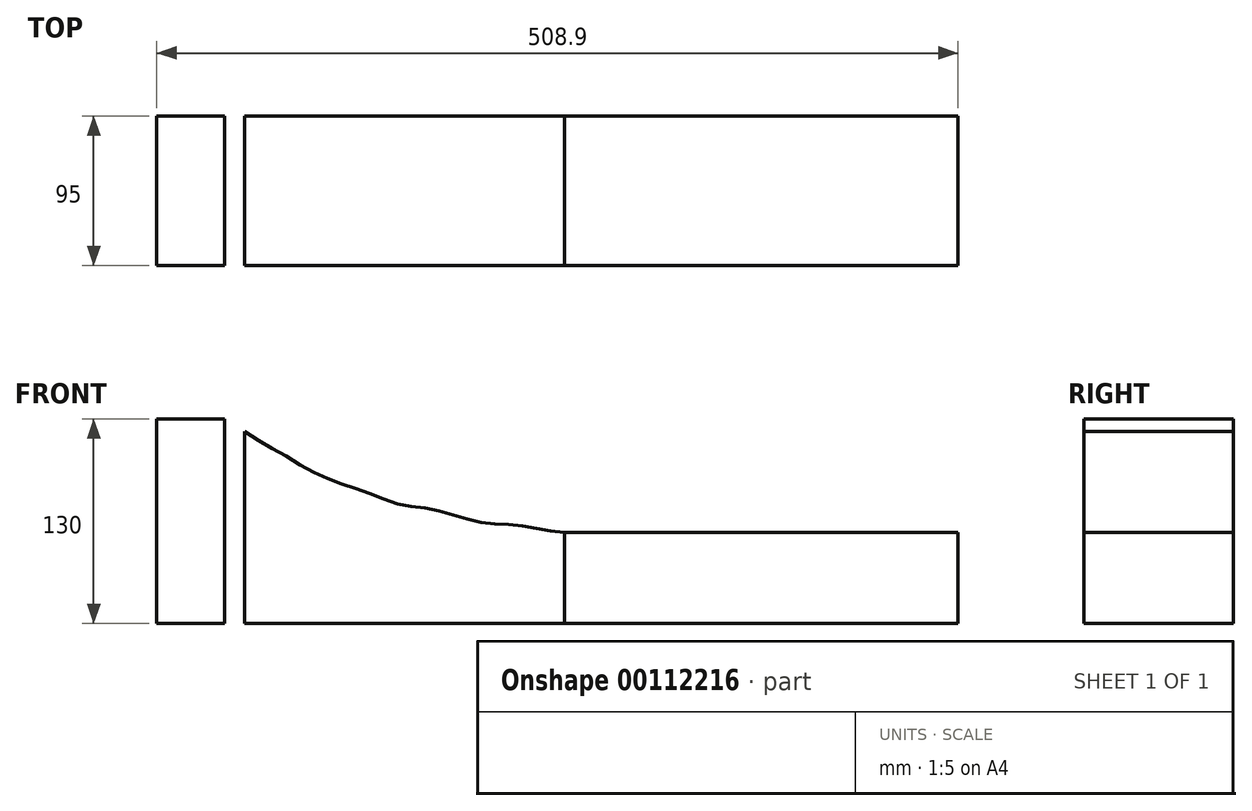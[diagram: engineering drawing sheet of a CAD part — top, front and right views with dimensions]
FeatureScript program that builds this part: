
annotation { "Feature Type Name" : "Feature", "Feature Type Description" : "" }
export const myFeature = defineFeature(function(context is Context, id is Id, definition is map)
    precondition{}
    {
        {
            var Q0;
            Q0=qCreatedBy(makeId("Right.planeOp"),FACE);
            var sketch = newSketch(context, id + "F0", { "sketchPlane" : qUnion([Q0])});
            skLineSegment(sketch, "E0.bottom", {"start": v(0, 0) * mm, "end": v(95, 0) * mm});
            skLineSegment(sketch, "E0.top", {"start": v(0, 130) * mm, "end": v(95, 130) * mm});
            skLineSegment(sketch, "E0.left", {"start": v(0, 0) * mm, "end": v(0, 130) * mm});
            skLineSegment(sketch, "E0.right", {"start": v(95, 0) * mm, "end": v(95, 130) * mm});
            skSolve(sketch);
        }
        {
            var Q0;
            Q0=makeQuery(id+"F0.imprint","IMPRINT",FACE,{"disambiguationData":[TD([[makeQuery(id+"F0.imprint","IMPRINT",EDGE,{"derivedFrom":sQuery(id+"F0.wireOp",EDGE,"E0.bottom")}),1.0]])]});
            cPlane(context, id + "F1", {"entities" : qUnion([Q0]), "cplaneType" : CPlaneType.OFFSET, "offset" : 12.7 * mm, "width" : 150 * mm, "height" : 150 * mm});
        }
        {
            var Q0;
            Q0=qCreatedBy(id+"F1.planeOp",FACE);
            cPlane(context, id + "F2", {"entities" : qUnion([Q0]), "cplaneType" : CPlaneType.OFFSET, "offset" : 12.7 * mm, "width" : 150 * mm, "height" : 150 * mm});
        }
        {
            var Q0;
            Q0=qCreatedBy(id+"F2.planeOp",FACE);
            cPlane(context, id + "F3", {"entities" : qUnion([Q0]), "cplaneType" : CPlaneType.OFFSET, "offset" : 12.7 * mm, "width" : 150 * mm, "height" : 150 * mm});
        }
        {
            var Q0;
            Q0=qCreatedBy(id+"F3.planeOp",FACE);
            cPlane(context, id + "F4", {"entities" : qUnion([Q0]), "cplaneType" : CPlaneType.OFFSET, "offset" : 12.7 * mm, "width" : 150 * mm, "height" : 150 * mm});
        }
        {
            var Q0;
            Q0=qCreatedBy(id+"F4.planeOp",FACE);
            cPlane(context, id + "F5", {"entities" : qUnion([Q0]), "cplaneType" : CPlaneType.OFFSET, "offset" : 12.7 * mm, "width" : 150 * mm, "height" : 150 * mm});
        }
        {
            var Q0;
            Q0=qCreatedBy(id+"F1.planeOp",FACE);
            var sketch = newSketch(context, id + "F6", { "sketchPlane" : qUnion([Q0])});
            skLineSegment(sketch, "E1.bottom", {"start": v(0, 0) * mm, "end": v(95, 0) * mm});
            skLineSegment(sketch, "E1.top", {"start": v(0, 122) * mm, "end": v(95, 122) * mm});
            skLineSegment(sketch, "E1.left", {"start": v(0, 0) * mm, "end": v(0, 122) * mm});
            skLineSegment(sketch, "E1.right", {"start": v(95, 0) * mm, "end": v(95, 122) * mm});
            skSolve(sketch);
        }
        {
            var Q0;
            Q0=qCreatedBy(id+"F2.planeOp",FACE);
            var sketch = newSketch(context, id + "F7", { "sketchPlane" : qUnion([Q0])});
            skLineSegment(sketch, "E2.bottom", {"start": v(0, 0) * mm, "end": v(95, 0) * mm});
            skLineSegment(sketch, "E2.top", {"start": v(0, 114) * mm, "end": v(95, 114) * mm});
            skLineSegment(sketch, "E2.left", {"start": v(0, 0) * mm, "end": v(0, 114) * mm});
            skLineSegment(sketch, "E2.right", {"start": v(95, 0) * mm, "end": v(95, 114) * mm});
            skSolve(sketch);
        }
        {
            var Q0;
            Q0=qCreatedBy(id+"F3.planeOp",FACE);
            var sketch = newSketch(context, id + "F8", { "sketchPlane" : qUnion([Q0])});
            skLineSegment(sketch, "E3.bottom", {"start": v(0, 0) * mm, "end": v(95, 0) * mm});
            skLineSegment(sketch, "E3.top", {"start": v(0, 107) * mm, "end": v(95, 107) * mm});
            skLineSegment(sketch, "E3.left", {"start": v(0, 0) * mm, "end": v(0, 107) * mm});
            skLineSegment(sketch, "E3.right", {"start": v(95, 0) * mm, "end": v(95, 107) * mm});
            skSolve(sketch);
        }
        {
            var Q0;
            Q0=qCreatedBy(id+"F4.planeOp",FACE);
            var sketch = newSketch(context, id + "F9", { "sketchPlane" : qUnion([Q0])});
            skLineSegment(sketch, "E4.bottom", {"start": v(0, 0) * mm, "end": v(95, 0) * mm});
            skLineSegment(sketch, "E4.top", {"start": v(0, 99) * mm, "end": v(95, 99) * mm});
            skLineSegment(sketch, "E4.left", {"start": v(0, 0) * mm, "end": v(0, 99) * mm});
            skLineSegment(sketch, "E4.right", {"start": v(95, 0) * mm, "end": v(95, 99) * mm});
            skSolve(sketch);
        }
        {
            var Q0;
            Q0=qCreatedBy(id+"F5.planeOp",FACE);
            var sketch = newSketch(context, id + "F10", { "sketchPlane" : qUnion([Q0])});
            skLineSegment(sketch, "E5.bottom", {"start": v(0, 0) * mm, "end": v(95, 0) * mm});
            skLineSegment(sketch, "E5.top", {"start": v(0, 93) * mm, "end": v(95, 93) * mm});
            skLineSegment(sketch, "E5.left", {"start": v(0, 0) * mm, "end": v(0, 93) * mm});
            skLineSegment(sketch, "E5.right", {"start": v(95, 0) * mm, "end": v(95, 93) * mm});
            skSolve(sketch);
        }
        {
            var Q0;
            Q0=qCreatedBy(id+"F5.planeOp",FACE);
            cPlane(context, id + "F11", {"entities" : qUnion([Q0]), "cplaneType" : CPlaneType.OFFSET, "offset" : 12.7 * mm, "width" : 150 * mm, "height" : 150 * mm});
        }
        {
            var Q0;
            Q0=qCreatedBy(id+"F11.planeOp",FACE);
            cPlane(context, id + "F12", {"entities" : qUnion([Q0]), "cplaneType" : CPlaneType.OFFSET, "offset" : 12.7 * mm, "width" : 150 * mm, "height" : 150 * mm});
        }
        {
            var Q0;
            Q0=qCreatedBy(id+"F12.planeOp",FACE);
            cPlane(context, id + "F13", {"entities" : qUnion([Q0]), "cplaneType" : CPlaneType.OFFSET, "offset" : 12.7 * mm, "width" : 150 * mm, "height" : 150 * mm});
        }
        {
            var Q0;
            Q0=qCreatedBy(id+"F11.planeOp",FACE);
            var sketch = newSketch(context, id + "F14", { "sketchPlane" : qUnion([Q0])});
            skLineSegment(sketch, "E6.bottom", {"start": v(0, 0) * mm, "end": v(95, 0) * mm});
            skLineSegment(sketch, "E6.top", {"start": v(0, 88) * mm, "end": v(95, 88) * mm});
            skLineSegment(sketch, "E6.left", {"start": v(0, 0) * mm, "end": v(0, 88) * mm});
            skLineSegment(sketch, "E6.right", {"start": v(95, 0) * mm, "end": v(95, 88) * mm});
            skSolve(sketch);
        }
        {
            var Q0;
            Q0=qCreatedBy(id+"F12.planeOp",FACE);
            var sketch = newSketch(context, id + "F15", { "sketchPlane" : qUnion([Q0])});
            skLineSegment(sketch, "E7.bottom", {"start": v(0, 0) * mm, "end": v(95, 0) * mm});
            skLineSegment(sketch, "E7.top", {"start": v(0, 84) * mm, "end": v(95, 84) * mm});
            skLineSegment(sketch, "E7.left", {"start": v(0, 0) * mm, "end": v(0, 84) * mm});
            skLineSegment(sketch, "E7.right", {"start": v(95, 0) * mm, "end": v(95, 84) * mm});
            skSolve(sketch);
        }
        {
            var Q0;
            Q0=qCreatedBy(id+"F13.planeOp",FACE);
            var sketch = newSketch(context, id + "F16", { "sketchPlane" : qUnion([Q0])});
            skLineSegment(sketch, "E8.bottom", {"start": v(0, 0) * mm, "end": v(95, 0) * mm});
            skLineSegment(sketch, "E8.top", {"start": v(0, 79) * mm, "end": v(95, 79) * mm});
            skLineSegment(sketch, "E8.left", {"start": v(0, 0) * mm, "end": v(0, 79) * mm});
            skLineSegment(sketch, "E8.right", {"start": v(95, 0) * mm, "end": v(95, 79) * mm});
            skSolve(sketch);
        }
        {
            var Q0;
            Q0=qCreatedBy(id+"F13.planeOp",FACE);
            cPlane(context, id + "F17", {"entities" : qUnion([Q0]), "cplaneType" : CPlaneType.OFFSET, "offset" : 12.7 * mm, "width" : 150 * mm, "height" : 150 * mm});
        }
        {
            var Q0;
            Q0=qCreatedBy(id+"F17.planeOp",FACE);
            cPlane(context, id + "F18", {"entities" : qUnion([Q0]), "cplaneType" : CPlaneType.OFFSET, "offset" : 12.7 * mm, "width" : 150 * mm, "height" : 150 * mm});
        }
        {
            var Q0;
            Q0=qCreatedBy(id+"F18.planeOp",FACE);
            cPlane(context, id + "F19", {"entities" : qUnion([Q0]), "cplaneType" : CPlaneType.OFFSET, "offset" : 12.7 * mm, "width" : 150 * mm, "height" : 150 * mm});
        }
        {
            var Q0;
            Q0=qCreatedBy(id+"F19.planeOp",FACE);
            cPlane(context, id + "F20", {"entities" : qUnion([Q0]), "cplaneType" : CPlaneType.OFFSET, "offset" : 12.7 * mm, "width" : 150 * mm, "height" : 150 * mm});
        }
        {
            var Q0;
            Q0=qCreatedBy(id+"F20.planeOp",FACE);
            cPlane(context, id + "F21", {"entities" : qUnion([Q0]), "cplaneType" : CPlaneType.OFFSET, "offset" : 12.7 * mm, "width" : 150 * mm, "height" : 150 * mm});
        }
        {
            var Q0;
            Q0=qCreatedBy(id+"F17.planeOp",FACE);
            var sketch = newSketch(context, id + "F22", { "sketchPlane" : qUnion([Q0])});
            skLineSegment(sketch, "E9.bottom", {"start": v(0, 0) * mm, "end": v(95, 0) * mm});
            skLineSegment(sketch, "E9.top", {"start": v(0, 75) * mm, "end": v(95, 75) * mm});
            skLineSegment(sketch, "E9.left", {"start": v(0, 0) * mm, "end": v(0, 75) * mm});
            skLineSegment(sketch, "E9.right", {"start": v(95, 0) * mm, "end": v(95, 75) * mm});
            skSolve(sketch);
        }
        {
            var Q0;
            Q0=qCreatedBy(id+"F18.planeOp",FACE);
            var sketch = newSketch(context, id + "F23", { "sketchPlane" : qUnion([Q0])});
            skLineSegment(sketch, "E10.bottom", {"start": v(0, 0) * mm, "end": v(95, 0) * mm});
            skLineSegment(sketch, "E10.top", {"start": v(0, 73.5) * mm, "end": v(95, 73.5) * mm});
            skLineSegment(sketch, "E10.left", {"start": v(0, 0) * mm, "end": v(0, 73.5) * mm});
            skLineSegment(sketch, "E10.right", {"start": v(95, 0) * mm, "end": v(95, 73.5) * mm});
            skSolve(sketch);
        }
        {
            var Q0;
            Q0=qCreatedBy(id+"F19.planeOp",FACE);
            var sketch = newSketch(context, id + "F24", { "sketchPlane" : qUnion([Q0])});
            skLineSegment(sketch, "E11.bottom", {"start": v(0, 0) * mm, "end": v(95, 0) * mm});
            skLineSegment(sketch, "E11.top", {"start": v(0, 70.5) * mm, "end": v(95, 70.5) * mm});
            skLineSegment(sketch, "E11.left", {"start": v(0, 0) * mm, "end": v(0, 70.5) * mm});
            skLineSegment(sketch, "E11.right", {"start": v(95, 0) * mm, "end": v(95, 70.5) * mm});
            skSolve(sketch);
        }
        {
            var Q0;
            Q0=qCreatedBy(id+"F20.planeOp",FACE);
            var sketch = newSketch(context, id + "F25", { "sketchPlane" : qUnion([Q0])});
            skLineSegment(sketch, "E12.bottom", {"start": v(0, 0) * mm, "end": v(95, 0) * mm});
            skLineSegment(sketch, "E12.top", {"start": v(0, 67) * mm, "end": v(95, 67) * mm});
            skLineSegment(sketch, "E12.left", {"start": v(0, 0) * mm, "end": v(0, 67) * mm});
            skLineSegment(sketch, "E12.right", {"start": v(95, 0) * mm, "end": v(95, 67) * mm});
            skSolve(sketch);
        }
        {
            var Q0;
            Q0=qCreatedBy(id+"F21.planeOp",FACE);
            var sketch = newSketch(context, id + "F26", { "sketchPlane" : qUnion([Q0])});
            skLineSegment(sketch, "E13.bottom", {"start": v(0, 0) * mm, "end": v(95, 0) * mm});
            skLineSegment(sketch, "E13.top", {"start": v(0, 64) * mm, "end": v(95, 64) * mm});
            skLineSegment(sketch, "E13.left", {"start": v(0, 0) * mm, "end": v(0, 64) * mm});
            skLineSegment(sketch, "E13.right", {"start": v(95, 0) * mm, "end": v(95, 64) * mm});
            skSolve(sketch);
        }
        {
            var Q0;
            Q0=qCreatedBy(id+"F21.planeOp",FACE);
            cPlane(context, id + "F27", {"entities" : qUnion([Q0]), "cplaneType" : CPlaneType.OFFSET, "offset" : 12.7 * mm, "width" : 150 * mm, "height" : 150 * mm});
        }
        {
            var Q0;
            Q0=qCreatedBy(id+"F27.planeOp",FACE);
            cPlane(context, id + "F28", {"entities" : qUnion([Q0]), "cplaneType" : CPlaneType.OFFSET, "offset" : 12.7 * mm, "width" : 150 * mm, "height" : 150 * mm});
        }
        {
            var Q0;
            Q0=qCreatedBy(id+"F28.planeOp",FACE);
            cPlane(context, id + "F29", {"entities" : qUnion([Q0]), "cplaneType" : CPlaneType.OFFSET, "offset" : 12.7 * mm, "width" : 150 * mm, "height" : 150 * mm});
        }
        {
            var Q0;
            Q0=qCreatedBy(id+"F29.planeOp",FACE);
            cPlane(context, id + "F30", {"entities" : qUnion([Q0]), "cplaneType" : CPlaneType.OFFSET, "offset" : 12.7 * mm, "width" : 150 * mm, "height" : 150 * mm});
        }
        {
            var Q0;
            Q0=qCreatedBy(id+"F27.planeOp",FACE);
            var sketch = newSketch(context, id + "F31", { "sketchPlane" : qUnion([Q0])});
            skLineSegment(sketch, "E14.bottom", {"start": v(0, 0) * mm, "end": v(95, 0) * mm});
            skLineSegment(sketch, "E14.top", {"start": v(0, 63) * mm, "end": v(95, 63) * mm});
            skLineSegment(sketch, "E14.left", {"start": v(0, 0) * mm, "end": v(0, 63) * mm});
            skLineSegment(sketch, "E14.right", {"start": v(95, 0) * mm, "end": v(95, 63) * mm});
            skSolve(sketch);
        }
        {
            var Q0;
            Q0=qCreatedBy(id+"F28.planeOp",FACE);
            var sketch = newSketch(context, id + "F32", { "sketchPlane" : qUnion([Q0])});
            skLineSegment(sketch, "E15.bottom", {"start": v(0, 0) * mm, "end": v(95, 0) * mm});
            skLineSegment(sketch, "E15.top", {"start": v(0, 62) * mm, "end": v(95, 62) * mm});
            skLineSegment(sketch, "E15.left", {"start": v(0, 0) * mm, "end": v(0, 62) * mm});
            skLineSegment(sketch, "E15.right", {"start": v(95, 0) * mm, "end": v(95, 62) * mm});
            skSolve(sketch);
        }
        {
            var Q0;
            Q0=qCreatedBy(id+"F29.planeOp",FACE);
            var sketch = newSketch(context, id + "F33", { "sketchPlane" : qUnion([Q0])});
            skLineSegment(sketch, "E16.bottom", {"start": v(0, 0) * mm, "end": v(95, 0) * mm});
            skLineSegment(sketch, "E16.top", {"start": v(0, 59.5) * mm, "end": v(95, 59.5) * mm});
            skLineSegment(sketch, "E16.left", {"start": v(0, 0) * mm, "end": v(0, 59.5) * mm});
            skLineSegment(sketch, "E16.right", {"start": v(95, 0) * mm, "end": v(95, 59.5) * mm});
            skSolve(sketch);
        }
        {
            var Q0;
            Q0=qCreatedBy(id+"F30.planeOp",FACE);
            var sketch = newSketch(context, id + "F34", { "sketchPlane" : qUnion([Q0])});
            skLineSegment(sketch, "E17.bottom", {"start": v(0, 0) * mm, "end": v(95, 0) * mm});
            skLineSegment(sketch, "E17.top", {"start": v(0, 58) * mm, "end": v(95, 58) * mm});
            skLineSegment(sketch, "E17.left", {"start": v(0, 0) * mm, "end": v(0, 58) * mm});
            skLineSegment(sketch, "E17.right", {"start": v(95, 0) * mm, "end": v(95, 58) * mm});
            skSolve(sketch);
        }
        {
            var Q0;
            Q0=makeQuery(id+"F0.imprint","IMPRINT",FACE,{"disambiguationData":[TD([[makeQuery(id+"F0.imprint","IMPRINT",EDGE,{"derivedFrom":sQuery(id+"F0.wireOp",EDGE,"E0.bottom")}),1.0]])]});
            extrude(context, id + "F35", {"entities" : qUnion([Q0]), "oppositeDirection" : true, "depth" : 43 * mm});
        }
        {
            var Q0;
            Q0=makeQuery(id+"F34.imprint","IMPRINT",FACE,{"disambiguationData":[TD([[makeQuery(id+"F34.imprint","IMPRINT",EDGE,{"derivedFrom":sQuery(id+"F34.wireOp",EDGE,"E17.bottom")}),1.0]])]});
            extrude(context, id + "F36", {"entities" : qUnion([Q0]), "depth" : 250 * mm});
        }
        {
            var Q0;
            Q0=makeQuery(id+"F6.imprint","IMPRINT",FACE,{"disambiguationData":[TD([[makeQuery(id+"F6.imprint","IMPRINT",EDGE,{"derivedFrom":sQuery(id+"F6.wireOp",EDGE,"E1.bottom")}),1.0]])]});
            var Q1;
            Q1=makeQuery(id+"F7.imprint","IMPRINT",FACE,{"disambiguationData":[TD([[makeQuery(id+"F7.imprint","IMPRINT",EDGE,{"derivedFrom":sQuery(id+"F7.wireOp",EDGE,"E2.bottom")}),1.0]])]});
            var Q2;
            Q2=makeQuery(id+"F8.imprint","IMPRINT",FACE,{"disambiguationData":[TD([[makeQuery(id+"F8.imprint","IMPRINT",EDGE,{"derivedFrom":sQuery(id+"F8.wireOp",EDGE,"E3.bottom")}),1.0]])]});
            var Q3;
            Q3=makeQuery(id+"F9.imprint","IMPRINT",FACE,{"disambiguationData":[TD([[makeQuery(id+"F9.imprint","IMPRINT",EDGE,{"derivedFrom":sQuery(id+"F9.wireOp",EDGE,"E4.bottom")}),1.0]])]});
            var Q4;
            Q4=makeQuery(id+"F10.imprint","IMPRINT",FACE,{"disambiguationData":[TD([[makeQuery(id+"F10.imprint","IMPRINT",EDGE,{"derivedFrom":sQuery(id+"F10.wireOp",EDGE,"E5.bottom")}),1.0]])]});
            var Q5;
            Q5=makeQuery(id+"F14.imprint","IMPRINT",FACE,{"disambiguationData":[TD([[makeQuery(id+"F14.imprint","IMPRINT",EDGE,{"derivedFrom":sQuery(id+"F14.wireOp",EDGE,"E6.bottom")}),1.0]])]});
            var Q6;
            Q6=makeQuery(id+"F15.imprint","IMPRINT",FACE,{"disambiguationData":[TD([[makeQuery(id+"F15.imprint","IMPRINT",EDGE,{"derivedFrom":sQuery(id+"F15.wireOp",EDGE,"E7.bottom")}),1.0]])]});
            var Q7;
            Q7=makeQuery(id+"F16.imprint","IMPRINT",FACE,{"disambiguationData":[TD([[makeQuery(id+"F16.imprint","IMPRINT",EDGE,{"derivedFrom":sQuery(id+"F16.wireOp",EDGE,"E8.bottom")}),1.0]])]});
            var Q8;
            Q8=makeQuery(id+"F22.imprint","IMPRINT",FACE,{"disambiguationData":[TD([[makeQuery(id+"F22.imprint","IMPRINT",EDGE,{"derivedFrom":sQuery(id+"F22.wireOp",EDGE,"E9.bottom")}),1.0]])]});
            var Q9;
            Q9=makeQuery(id+"F23.imprint","IMPRINT",FACE,{"disambiguationData":[TD([[makeQuery(id+"F23.imprint","IMPRINT",EDGE,{"derivedFrom":sQuery(id+"F23.wireOp",EDGE,"E10.bottom")}),1.0]])]});
            var Q10;
            Q10=makeQuery(id+"F24.imprint","IMPRINT",FACE,{"disambiguationData":[TD([[makeQuery(id+"F24.imprint","IMPRINT",EDGE,{"derivedFrom":sQuery(id+"F24.wireOp",EDGE,"E11.bottom")}),1.0]])]});
            var Q11;
            Q11=makeQuery(id+"F25.imprint","IMPRINT",FACE,{"disambiguationData":[TD([[makeQuery(id+"F25.imprint","IMPRINT",EDGE,{"derivedFrom":sQuery(id+"F25.wireOp",EDGE,"E12.bottom")}),1.0]])]});
            var Q12;
            Q12=makeQuery(id+"F26.imprint","IMPRINT",FACE,{"disambiguationData":[TD([[makeQuery(id+"F26.imprint","IMPRINT",EDGE,{"derivedFrom":sQuery(id+"F26.wireOp",EDGE,"E13.bottom")}),1.0]])]});
            var Q13;
            Q13=makeQuery(id+"F31.imprint","IMPRINT",FACE,{"disambiguationData":[TD([[makeQuery(id+"F31.imprint","IMPRINT",EDGE,{"derivedFrom":sQuery(id+"F31.wireOp",EDGE,"E14.bottom")}),1.0]])]});
            var Q14;
            Q14=makeQuery(id+"F32.imprint","IMPRINT",FACE,{"disambiguationData":[TD([[makeQuery(id+"F32.imprint","IMPRINT",EDGE,{"derivedFrom":sQuery(id+"F32.wireOp",EDGE,"E15.bottom")}),1.0]])]});
            var Q15;
            Q15=makeQuery(id+"F33.imprint","IMPRINT",FACE,{"disambiguationData":[TD([[makeQuery(id+"F33.imprint","IMPRINT",EDGE,{"derivedFrom":sQuery(id+"F33.wireOp",EDGE,"E16.bottom")}),1.0]])]});
            var Q16;
            Q16=makeQuery(id+"F36.opExtrude","CAP_FACE",FACE,{"disambiguationData":[OSD([sQuery(id+"F34.wireOp",EDGE,"E17.bottom"),sQuery(id+"F34.wireOp",EDGE,"E17.top"),sQuery(id+"F34.wireOp",EDGE,"E17.left"),sQuery(id+"F34.wireOp",EDGE,"E17.right")])],"isStart":true});
            loft(context, id + "F37", {"sheetProfilesArray" : [{ "sheetProfileEntities" : qUnion([Q0]) }, { "sheetProfileEntities" : qUnion([Q1]) }, { "sheetProfileEntities" : qUnion([Q2]) }, { "sheetProfileEntities" : qUnion([Q3]) }, { "sheetProfileEntities" : qUnion([Q4]) }, { "sheetProfileEntities" : qUnion([Q5]) }, { "sheetProfileEntities" : qUnion([Q6]) }, { "sheetProfileEntities" : qUnion([Q7]) }, { "sheetProfileEntities" : qUnion([Q8]) }, { "sheetProfileEntities" : qUnion([Q9]) }, { "sheetProfileEntities" : qUnion([Q10]) }, { "sheetProfileEntities" : qUnion([Q11]) }, { "sheetProfileEntities" : qUnion([Q12]) }, { "sheetProfileEntities" : qUnion([Q13]) }, { "sheetProfileEntities" : qUnion([Q14]) }, { "sheetProfileEntities" : qUnion([Q15]) }, { "sheetProfileEntities" : qUnion([Q16]) }]});
        }
    });
